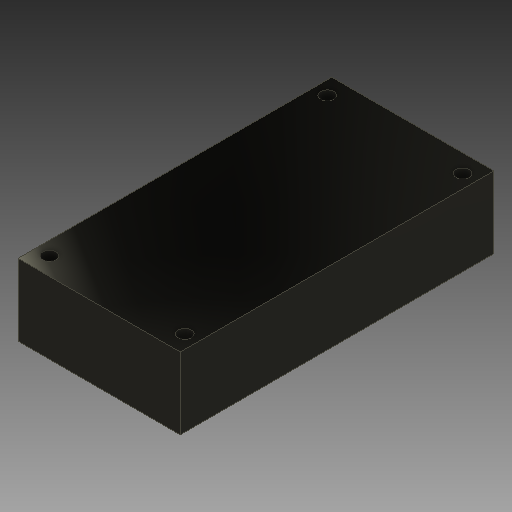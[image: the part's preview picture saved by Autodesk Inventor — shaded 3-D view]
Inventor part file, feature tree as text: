
AUTODESK INVENTOR PART (.ipt)
format: ipt  version: 2020 (Build 240168000, 168)  size: 108,032 bytes
history: native  units: mm
features: other x2, extrude x1, sketch x1
ambient origin geometry x8: Origin, YZ Plane, XZ Plane, XY Plane, X Axis, Y Axis, Z Axis, Center Point
bodies: Body1 (feature_tree)
feature tree (4):
  other  "boost"
  other  "Твердое тело1"
  extrude  "Выдавливание1"  Depth=36.2mm
  sketch  "Эскиз1"
